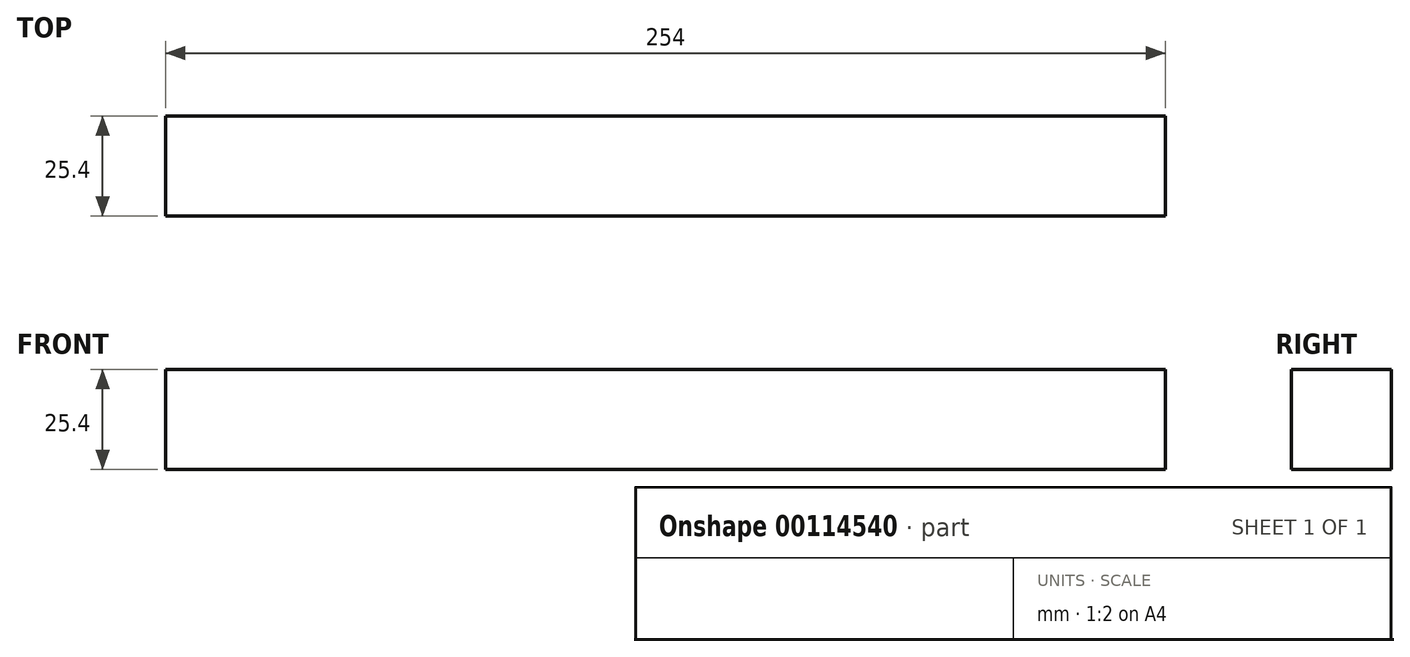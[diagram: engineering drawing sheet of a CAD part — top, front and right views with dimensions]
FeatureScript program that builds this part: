
annotation { "Feature Type Name" : "Feature", "Feature Type Description" : "" }
export const myFeature = defineFeature(function(context is Context, id is Id, definition is map)
    precondition{}
    {
        {
            var Q0;
            Q0=qCreatedBy(makeId("Top.planeOp"),FACE);
            var sketch = newSketch(context, id + "F0", { "sketchPlane" : qUnion([Q0])});
            skLineSegment(sketch, "E0.bottom", {"start": v(-24.63, 7.67) * mm, "end": v(229.37, 7.67) * mm});
            skLineSegment(sketch, "E0.top", {"start": v(-24.63, -17.73) * mm, "end": v(229.37, -17.73) * mm});
            skLineSegment(sketch, "E0.left", {"start": v(-24.63, 7.67) * mm, "end": v(-24.63, -17.73) * mm});
            skLineSegment(sketch, "E0.right", {"start": v(229.37, 7.67) * mm, "end": v(229.37, -17.73) * mm});
            skSolve(sketch);
        }
        {
            var Q0;
            Q0=sQuery(id+"F0.wireOp",EDGE,"E0.top");
            var Q1;
            Q1=sQuery(id+"F0.wireOp",EDGE,"E0.bottom");
            var Q2;
            Q2=sQuery(id+"F0.wireOp",EDGE,"E0.left");
            var Q3;
            Q3=sQuery(id+"F0.wireOp",EDGE,"E0.right");
            extrude(context, id + "F1", {"bodyType" : ToolBodyType.SURFACE, "surfaceEntities" : qUnion([Q0, Q1, Q2, Q3]), "oppositeDirection" : true, "depth" : 25.4 * mm});
        }
    });
